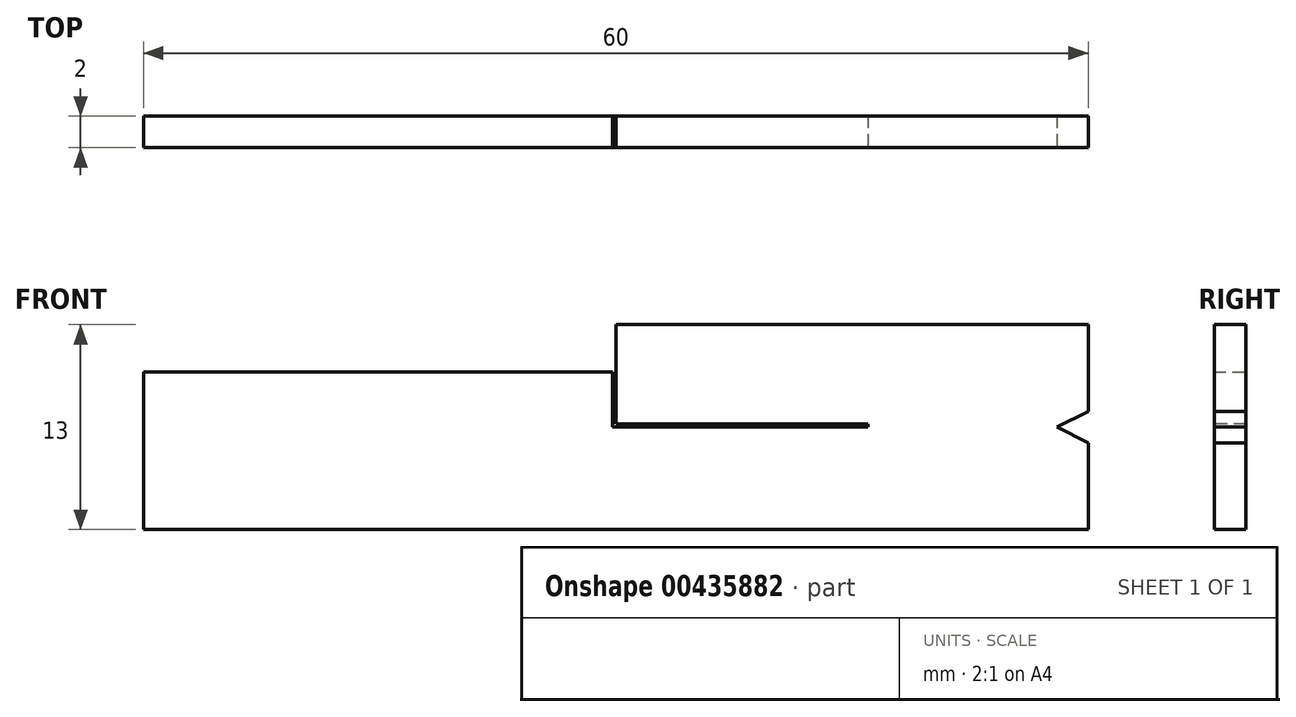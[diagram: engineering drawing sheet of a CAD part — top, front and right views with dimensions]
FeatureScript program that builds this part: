
annotation { "Feature Type Name" : "Feature", "Feature Type Description" : "" }
export const myFeature = defineFeature(function(context is Context, id is Id, definition is map)
    precondition{}
    {
        {
            var Q0;
            Q0=qCreatedBy(makeId("Front.planeOp"),FACE);
            var sketch = newSketch(context, id + "F0", { "sketchPlane" : qUnion([Q0])});
            skLineSegment(sketch, "E0.bottom", {"start": v(0, 0) * mm, "end": v(60, 0) * mm});
            skLineSegment(sketch, "E0.top", {"start": v(0, 10) * mm, "end": v(60, 10) * mm});
            skLineSegment(sketch, "E0.left", {"start": v(0, 0) * mm, "end": v(0, 10) * mm});
            skLineSegment(sketch, "E0.right", {"start": v(60, 0) * mm, "end": v(60, 10) * mm});
            skSolve(sketch);
        }
        {
            var Q0;
            Q0 = qSketchRegion(id + "F0", true);
            extrude(context, id + "F1", {"entities" : qUnion([Q0]), "depth" : 2 * mm});
        }
        {
            var Q0;
            Q0=makeQuery(id+"F1.opExtrude","CAP_FACE",FACE,{"disambiguationData":[OSD([sQuery(id+"F0.wireOp",EDGE,"E0.bottom"),sQuery(id+"F0.wireOp",EDGE,"E0.top"),sQuery(id+"F0.wireOp",EDGE,"E0.left"),sQuery(id+"F0.wireOp",EDGE,"E0.right")])],"isStart":false});
            var sketch = newSketch(context, id + "F2", { "sketchPlane" : qUnion([Q0])});
            skLineSegment(sketch, "E1.bottom", {"start": v(60, 10) * mm, "end": v(30, 10) * mm});
            skLineSegment(sketch, "E1.top", {"start": v(60, 13) * mm, "end": v(30, 13) * mm});
            skLineSegment(sketch, "E1.left", {"start": v(60, 10) * mm, "end": v(60, 13) * mm});
            skLineSegment(sketch, "E1.right", {"start": v(30, 10) * mm, "end": v(30, 13) * mm});
            skSolve(sketch);
        }
        {
            var Q0;
            Q0 = qSketchRegion(id + "F2", true);
            var Q1;
            Q1=makeQuery(id+"F1.opExtrude","CAP_FACE",FACE,{"disambiguationData":[OSD([sQuery(id+"F0.wireOp",EDGE,"E0.bottom"),sQuery(id+"F0.wireOp",EDGE,"E0.top"),sQuery(id+"F0.wireOp",EDGE,"E0.left"),sQuery(id+"F0.wireOp",EDGE,"E0.right")])],"isStart":true});
            extrude(context, id + "F3", {"entities" : qUnion([Q0]), "operationType" : NewBodyOperationType.ADD, "endBound" : BoundingType.UP_TO_SURFACE, "oppositeDirection" : true, "endBoundEntityFace" : qUnion([Q1]), "depth" : 25 * mm});
        }
        {
            var Q0;
            Q0=makeQuery(id+"F3.boolean.opBoolean","MERGE",FACE,{"derivedFrom":[makeQuery(id+"F1.opExtrude","CAP_FACE",FACE,{"disambiguationData":[OSD([sQuery(id+"F0.wireOp",EDGE,"E0.bottom"),sQuery(id+"F0.wireOp",EDGE,"E0.top"),sQuery(id+"F0.wireOp",EDGE,"E0.left"),sQuery(id+"F0.wireOp",EDGE,"E0.right")])],"isStart":false}),makeQuery(id+"F3.opExtrude","CAP_FACE",FACE,{"disambiguationData":[OSD([sQuery(id+"F2.wireOp",EDGE,"E1.bottom"),sQuery(id+"F2.wireOp",EDGE,"E1.top"),sQuery(id+"F2.wireOp",EDGE,"E1.left"),sQuery(id+"F2.wireOp",EDGE,"E1.right")])],"isStart":true})]});
            var sketch = newSketch(context, id + "F4", { "sketchPlane" : qUnion([Q0])});
            skLineSegment(sketch, "E2", {"start": v(60, 7.5) * mm, "end": v(58, 6.5) * mm});
            skLineSegment(sketch, "E3", {"start": v(58, 6.5) * mm, "end": v(60, 5.5) * mm});
            skLineSegment(sketch, "E4", {"start": v(60, 5.5) * mm, "end": v(60, 7.5) * mm});
            skLineSegment(sketch, "E5", {"start": v(60, 6.5) * mm, "end": v(58, 6.5) * mm, "construction": true});
            skLineSegment(sketch, "E6", {"start": v(30, 10) * mm, "end": v(30, 6.7) * mm});
            skLineSegment(sketch, "E7", {"start": v(30, 6.7) * mm, "end": v(46, 6.7) * mm});
            skLineSegment(sketch, "E8.0", {"start": v(29.8, 6.5) * mm, "end": v(46, 6.5) * mm});
            skLineSegment(sketch, "E8.1", {"start": v(29.8, 10) * mm, "end": v(29.8, 6.5) * mm});
            skLineSegment(sketch, "E9", {"start": v(30, 10) * mm, "end": v(29.8, 10) * mm});
            skLineSegment(sketch, "E10", {"start": v(46, 6.7) * mm, "end": v(46, 6.5) * mm});
            skLineSegment(sketch, "E11", {"start": v(46, 6.5) * mm, "end": v(58, 6.5) * mm, "construction": true});
            skSolve(sketch);
        }
        {
            var Q0;
            Q0 = qSketchRegion(id + "F4", true);
            extrude(context, id + "F5", {"entities" : qUnion([Q0]), "operationType" : NewBodyOperationType.REMOVE, "endBound" : BoundingType.THROUGH_ALL, "oppositeDirection" : true, "depth" : 25 * mm});
        }
    });
